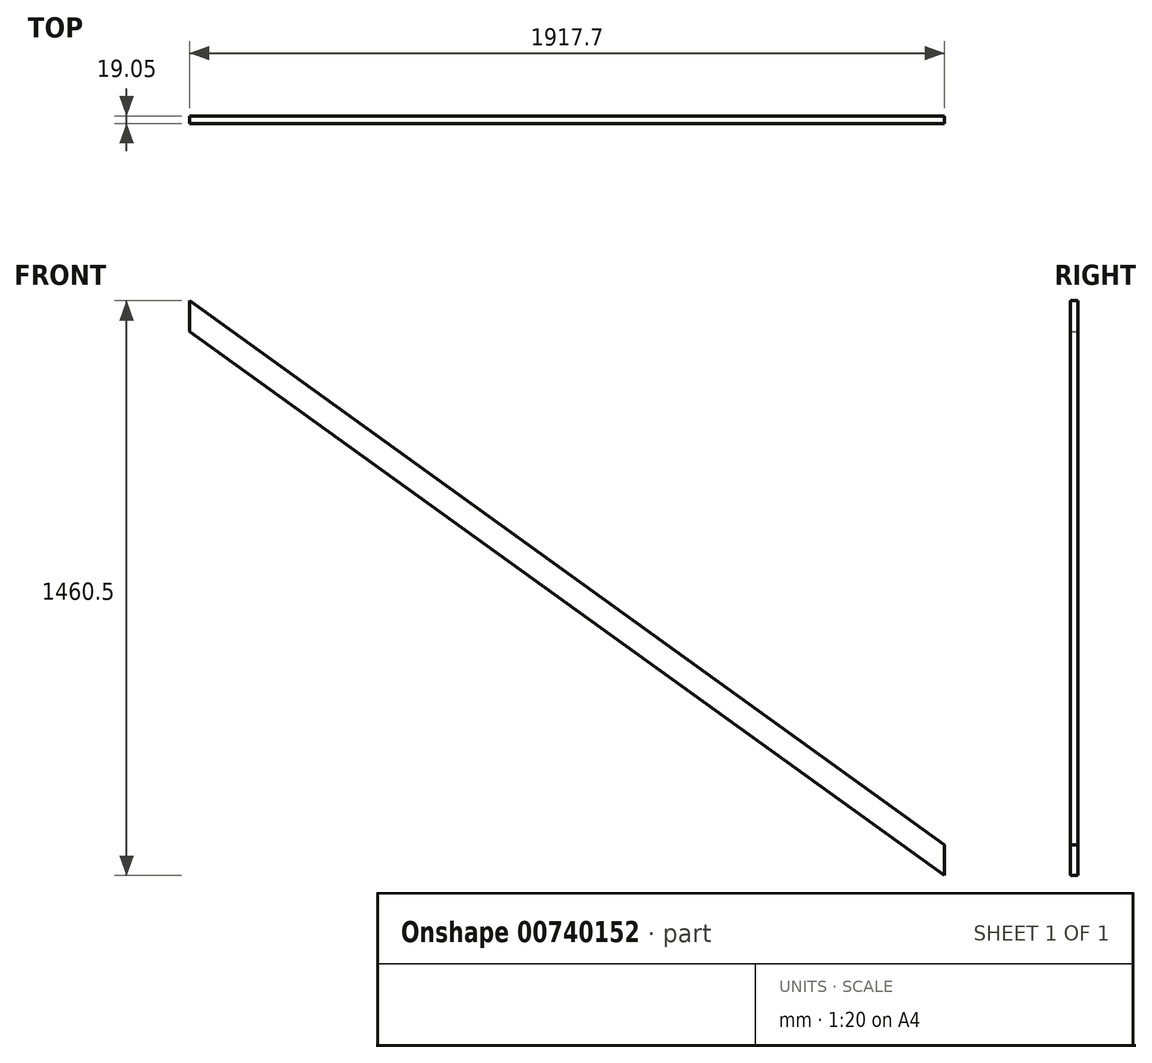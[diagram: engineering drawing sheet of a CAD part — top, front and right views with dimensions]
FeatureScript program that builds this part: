
annotation { "Feature Type Name" : "Feature", "Feature Type Description" : "" }
export const myFeature = defineFeature(function(context is Context, id is Id, definition is map)
    precondition{}
    {
        {
            var Q0;
            Q0=qCreatedBy(makeId("Front.planeOp"),FACE);
            var sketch = newSketch(context, id + "F0", { "sketchPlane" : qUnion([Q0])});
            skLineSegment(sketch, "E0.bottom", {"start": v(-761.83, 687.7) * mm, "end": v(1155.87, 687.7) * mm});
            skLineSegment(sketch, "E0.top", {"start": v(-761.83, -772.8) * mm, "end": v(1155.87, -772.8) * mm});
            skLineSegment(sketch, "E0.left", {"start": v(-761.83, 687.7) * mm, "end": v(-761.83, -772.8) * mm});
            skLineSegment(sketch, "E0.right", {"start": v(1155.87, 687.7) * mm, "end": v(1155.87, -772.8) * mm});
            skLineSegment(sketch, "E1.bottom", {"start": v(-761.83, 687.7) * mm, "end": v(1193, -721.29) * mm});
            skLineSegment(sketch, "E1.top", {"start": v(-798.96, 636.19) * mm, "end": v(1155.87, -772.8) * mm});
            skLineSegment(sketch, "E1.left", {"start": v(-761.83, 687.7) * mm, "end": v(-798.96, 636.19) * mm});
            skLineSegment(sketch, "E1.right", {"start": v(1193, -721.29) * mm, "end": v(1155.87, -772.8) * mm});
            skPoint(sketch, "E1.middle", {"position": v(197.02, -42.55) * mm});
            skPoint(sketch, "E1.middle.positionSnap0", {"position": v(197.02, 687.7) * mm});
            skPoint(sketch, "E1.middle.positionSnap1", {"position": v(-761.83, -42.55) * mm});
            skPoint(sketch, "E1.centerSnap0", {"position": v(197.02, 687.7) * mm});
            skPoint(sketch, "E1.centerSnap1", {"position": v(-761.83, -42.55) * mm});
            skSolve(sketch);
        }
        {
            var Q0;
            {var subQ1=sQuery(id+"F0.wireOp",EDGE,"E0.left");var subQ3=sQuery(id+"F0.wireOp",EDGE,"E1.top");var subQ4=makeQuery(id+"F0.imprint","INTERSECT",VERTEX,{"derivedFrom":[subQ1,subQ3]});Q0=makeQuery(id+"F0.imprint","IMPRINT",FACE,{"disambiguationData":[TD([[makeQuery(id+"F0.imprint","IMPRINT",EDGE,{"disambiguationData":[TD([[subQ4,1.0]])],"derivedFrom":subQ1}),1.0]])]});}
            extrude(context, id + "F1", {"entities" : qUnion([Q0]), "depth" : 19.05 * mm, "offsetDistance" : 25.4 * mm});
        }
    });
